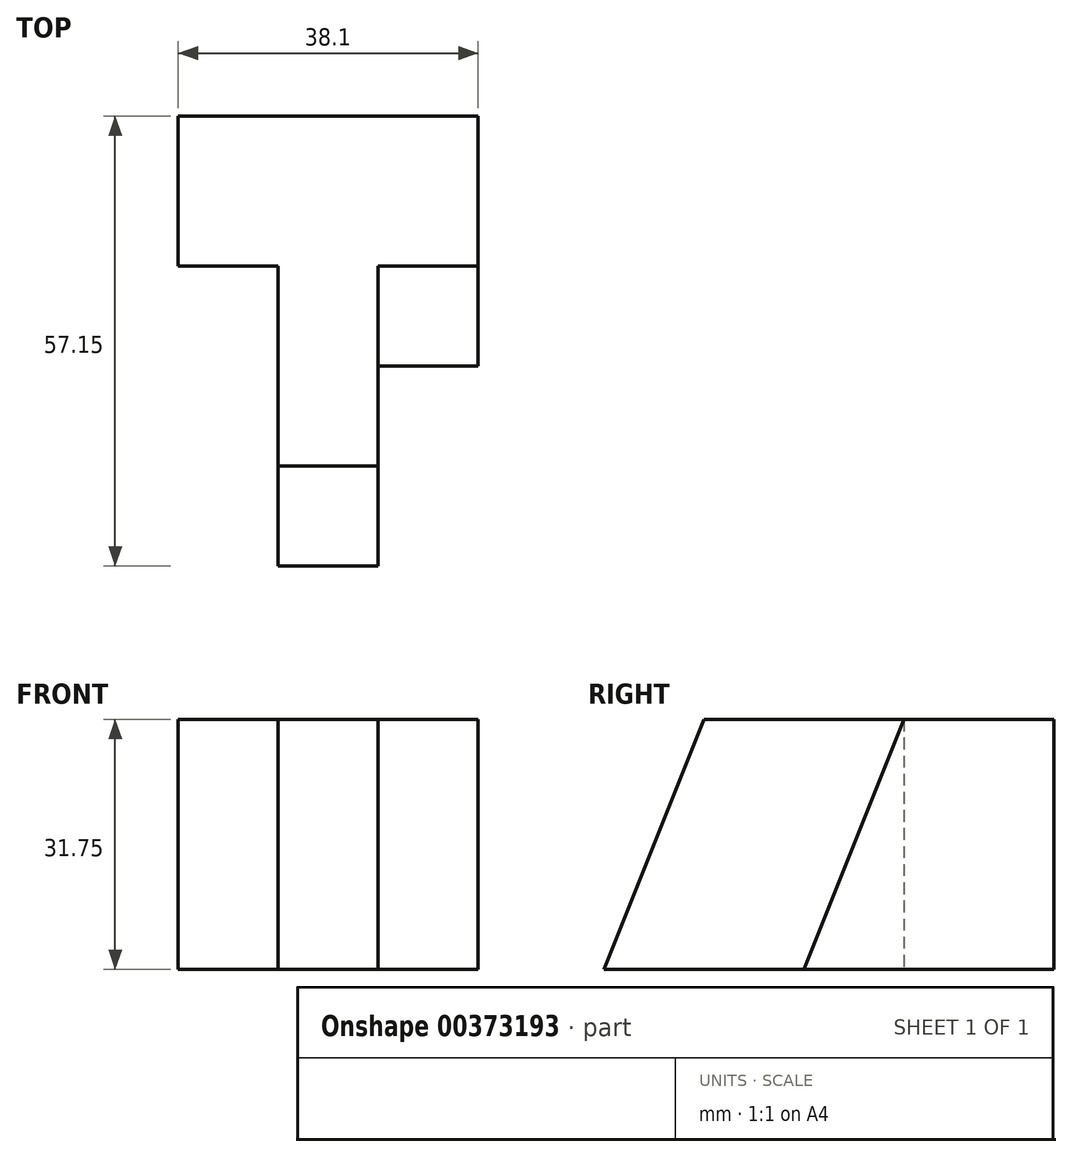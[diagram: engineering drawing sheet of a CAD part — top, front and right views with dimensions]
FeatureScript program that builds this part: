
annotation { "Feature Type Name" : "Feature", "Feature Type Description" : "" }
export const myFeature = defineFeature(function(context is Context, id is Id, definition is map)
    precondition{}
    {
        {
            var Q0;
            Q0=qCreatedBy(makeId("Top.planeOp"),FACE);
            var sketch = newSketch(context, id + "F0", { "sketchPlane" : qUnion([Q0])});
            skLineSegment(sketch, "E0", {"start": v(-19.72, 44.45) * mm, "end": v(18.38, 44.45) * mm});
            skLineSegment(sketch, "E1", {"start": v(18.38, 44.45) * mm, "end": v(18.38, 25.4) * mm});
            skLineSegment(sketch, "E2", {"start": v(18.38, 25.4) * mm, "end": v(5.68, 25.4) * mm});
            skLineSegment(sketch, "E3", {"start": v(5.68, 25.4) * mm, "end": v(5.68, 0) * mm});
            skLineSegment(sketch, "E4", {"start": v(5.68, 0) * mm, "end": v(-7.02, 0) * mm});
            skLineSegment(sketch, "E5", {"start": v(-7.02, 0) * mm, "end": v(-7.02, 25.4) * mm});
            skLineSegment(sketch, "E6", {"start": v(-7.02, 25.4) * mm, "end": v(-19.72, 25.4) * mm});
            skLineSegment(sketch, "E7", {"start": v(-19.72, 25.4) * mm, "end": v(-19.72, 44.45) * mm});
            skSolve(sketch);
        }
        {
            var Q0;
            Q0 = qSketchRegion(id + "F0", true);
            extrude(context, id + "F1", {"entities" : qUnion([Q0]), "depth" : 31.75 * mm});
        }
        {
            var Q0;
            Q0=makeQuery(id+"F1.opExtrude","SWEPT_FACE",FACE,{"disambiguationData":[OSD([sQuery(id+"F0.wireOp",EDGE,"E3")])]});
            var sketch = newSketch(context, id + "F2", { "sketchPlane" : qUnion([Q0])});
            skLineSegment(sketch, "E8", {"start": v(25.4, 0) * mm, "end": v(12.7, 0) * mm});
            skLineSegment(sketch, "E9", {"start": v(12.7, 0) * mm, "end": v(25.4, 31.75) * mm});
            skSolve(sketch);
        }
        {
            var Q0;
            Q0 = qSketchRegion(id + "F2", true);
            var Q1;
            Q1=makeQuery(id+"F2.imprint","IMPRINT",FACE,{"disambiguationData":[TD([[makeQuery(id+"F2.imprint","IMPRINT",EDGE,{"derivedFrom":sQuery(id+"F2.wireOp",EDGE,"E8")}),-1.0]])]});
            extrude(context, id + "F3", {"entities" : qUnion([Q0, Q1]), "operationType" : NewBodyOperationType.ADD, "depth" : 12.7 * mm});
        }
        {
            var Q0;
            Q0=makeQuery(id+"F1.opExtrude","SWEPT_FACE",FACE,{"disambiguationData":[OSD([sQuery(id+"F0.wireOp",EDGE,"E3")])]});
            var sketch = newSketch(context, id + "F4", { "sketchPlane" : qUnion([Q0])});
            skLineSegment(sketch, "E10", {"start": v(0, 0) * mm, "end": v(-12.7, 0) * mm});
            skLineSegment(sketch, "E11", {"start": v(-12.7, 0) * mm, "end": v(0, 31.75) * mm});
            skSolve(sketch);
        }
        {
            var Q0;
            Q0=makeQuery(id+"F4.imprint","IMPRINT",FACE,{"disambiguationData":[TD([[makeQuery(id+"F4.imprint","IMPRINT",EDGE,{"derivedFrom":sQuery(id+"F4.wireOp",EDGE,"E10")}),-1.0]])]});
            extrude(context, id + "F5", {"entities" : qUnion([Q0]), "operationType" : NewBodyOperationType.ADD, "oppositeDirection" : true, "depth" : 12.7 * mm});
        }
    });
